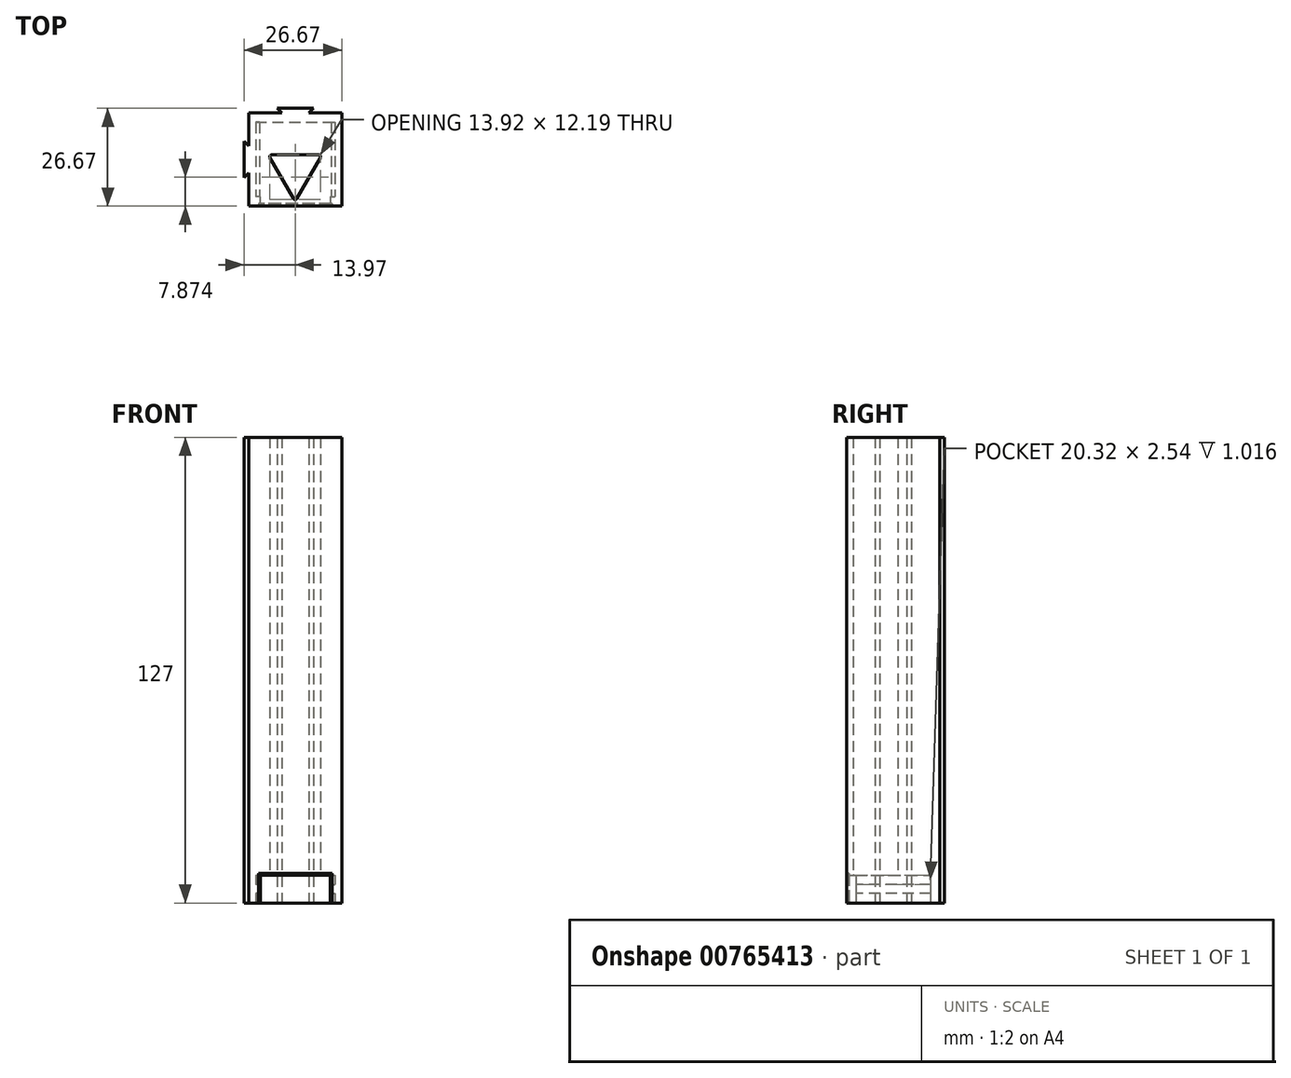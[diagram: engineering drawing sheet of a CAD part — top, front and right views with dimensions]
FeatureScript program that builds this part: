
annotation { "Feature Type Name" : "Feature", "Feature Type Description" : "" }
export const myFeature = defineFeature(function(context is Context, id is Id, definition is map)
    precondition{}
    {
        {
            var Q0;
            Q0=qCreatedBy(makeId("Top.planeOp"),FACE);
            var sketch = newSketch(context, id + "F0", { "sketchPlane" : qUnion([Q0])});
            skLineSegment(sketch, "E0.bottom", {"start": v(12.7, 12.7) * mm, "end": v(-12.7, 12.7) * mm});
            skLineSegment(sketch, "E0.top", {"start": v(12.7, -12.7) * mm, "end": v(-12.7, -12.7) * mm});
            skLineSegment(sketch, "E0.left", {"start": v(12.7, 12.7) * mm, "end": v(12.7, -12.7) * mm});
            skLineSegment(sketch, "E0.right", {"start": v(-12.7, 12.7) * mm, "end": v(-12.7, -12.7) * mm});
            skPoint(sketch, "E0.middle", {"position": v(0, 0) * mm});
            skLineSegment(sketch, "E1", {"start": v(-3.68, 12.7) * mm, "end": v(-4.95, 13.97) * mm});
            skLineSegment(sketch, "E2", {"start": v(-4.95, 13.97) * mm, "end": v(4.95, 13.97) * mm});
            skLineSegment(sketch, "E3", {"start": v(4.95, 13.97) * mm, "end": v(3.68, 12.7) * mm});
            skLineSegment(sketch, "E4.MirrorCS", {"start": v(-12.7, 3.68) * mm, "end": v(-13.97, 4.95) * mm});
            skLineSegment(sketch, "E5.MirrorCS", {"start": v(-13.97, 4.95) * mm, "end": v(-13.97, -4.95) * mm});
            skLineSegment(sketch, "E6.MirrorCS", {"start": v(-13.97, -4.95) * mm, "end": v(-12.7, -3.68) * mm});
            skLineSegment(sketch, "E7.top", {"start": v(-6.45, 1.27) * mm, "end": v(6.45, 1.27) * mm});
            skPoint(sketch, "E7.middle", {"position": v(0, -5.08) * mm});
            skPoint(sketch, "E8.visualSharp", {"position": v(0, 1.27) * mm});
            skLineSegment(sketch, "E9", {"start": v(-0.44, -10.67) * mm, "end": v(-6.9, 0.5) * mm});
            skLineSegment(sketch, "E10", {"start": v(0.44, -10.67) * mm, "end": v(6.9, 0.5) * mm});
            skPoint(sketch, "E7.left.start.orphan", {"position": v(-7.33, -11.43) * mm});
            skPoint(sketch, "E7.right.start.orphan", {"position": v(7.33, -11.43) * mm});
            skPoint(sketch, "E11.visualSharp", {"position": v(0, -11.43) * mm});
            skArc(sketch, "E11.filletArc", {"start": v(-0.44, -10.67) * mm, "mid": v(0, -10.92) * mm, "end": v(0.44, -10.67) * mm});
            skPoint(sketch, "E12.visualSharp", {"position": v(-7.33, 1.27) * mm});
            skArc(sketch, "E12.filletArc", {"start": v(-6.45, 1.27) * mm, "mid": v(-6.9, 1.02) * mm, "end": v(-6.9, 0.5) * mm});
            skPoint(sketch, "E13.visualSharp", {"position": v(7.33, 1.27) * mm});
            skArc(sketch, "E13.filletArc", {"start": v(6.9, 0.5) * mm, "mid": v(6.9, 1.02) * mm, "end": v(6.45, 1.27) * mm});
            skSolve(sketch);
        }
        {
            var Q0;
            {var subQ1=sQuery(id+"F0.wireOp",EDGE,"E0.top");Q0=makeQuery(id+"F0.imprint","IMPRINT",FACE,{"disambiguationData":[TD([[makeQuery(id+"F0.imprint","IMPRINT",EDGE,{"derivedFrom":subQ1}),-1.0]])]});}
            var Q1;
            {var subQ0=sQuery(id+"F0.wireOp",EDGE,"E4.MirrorCS");Q1=makeQuery(id+"F0.imprint","IMPRINT",FACE,{"disambiguationData":[TD([[makeQuery(id+"F0.imprint","IMPRINT",EDGE,{"derivedFrom":subQ0}),1.0]])]});}
            var Q2;
            {var subQ0=sQuery(id+"F0.wireOp",EDGE,"995b501b-87b1-40df-89db-5718103b703a");Q2=makeQuery(id+"F0.imprint","IMPRINT",FACE,{"disambiguationData":[TD([[makeQuery(id+"F0.imprint","IMPRINT",EDGE,{"derivedFrom":subQ0}),-1.0]])]});}
            var Q3;
            {var subQ0=sQuery(id+"F0.wireOp",EDGE,"E1");Q3=makeQuery(id+"F0.imprint","IMPRINT",FACE,{"disambiguationData":[TD([[makeQuery(id+"F0.imprint","IMPRINT",EDGE,{"derivedFrom":subQ0}),-1.0]])]});}
            var Q4;
            Q4=makeQuery(id+"F0.imprint","IMPRINT",FACE,{"disambiguationData":[TD([[makeQuery(id+"F0.imprint","IMPRINT",EDGE,{"derivedFrom":sQuery(id+"F0.wireOp",EDGE,"E7.bottom")}),1.0]])]});
            var Q5;
            Q5=makeQuery(id+"F0.imprint","IMPRINT",FACE,{"disambiguationData":[TD([[makeQuery(id+"F0.imprint","IMPRINT",EDGE,{"derivedFrom":sQuery(id+"F0.wireOp",EDGE,"311fc631-adf6-4f6f-8443-b1374ca45b62.0")}),-1.0]])]});
            extrude(context, id + "F1", {"entities" : qUnion([Q0, Q1, Q2, Q3, Q4, Q5]), "depth" : 127 * mm, "offsetDistance" : 25.4 * mm});
        }
        {
            var Q0;
            Q0=makeQuery(id+"F1.opExtrude","CAP_FACE",FACE,{"disambiguationData":[OSD([sQuery(id+"F0.wireOp",EDGE,"E0.bottom"),sQuery(id+"F0.wireOp",EDGE,"E0.top"),sQuery(id+"F0.wireOp",EDGE,"E0.left"),sQuery(id+"F0.wireOp",EDGE,"E0.right"),sQuery(id+"F0.wireOp",EDGE,"E1"),sQuery(id+"F0.wireOp",EDGE,"E2"),sQuery(id+"F0.wireOp",EDGE,"E3"),sQuery(id+"F0.wireOp",EDGE,"995b501b-87b1-40df-89db-5718103b703a"),sQuery(id+"F0.wireOp",EDGE,"d9b632a0-34b0-463a-8696-1e9d1799fc8a"),sQuery(id+"F0.wireOp",EDGE,"b3bc504c-1797-48d5-8887-40c9249a8113"),sQuery(id+"F0.wireOp",EDGE,"E4.MirrorCS"),sQuery(id+"F0.wireOp",EDGE,"E5.MirrorCS"),sQuery(id+"F0.wireOp",EDGE,"E6.MirrorCS"),sQuery(id+"F0.wireOp",EDGE,"Ek69CNRn-8RVK-RxQl-53fH-Jz5PkY7OIrkr")])],"isStart":true});
            var sketch = newSketch(context, id + "F2", { "sketchPlane" : qUnion([Q0])});
            skLineSegment(sketch, "E14", {"start": v(-9.52, 12.7) * mm, "end": v(-9.52, 10.16) * mm});
            skLineSegment(sketch, "E15", {"start": v(-9.52, 10.16) * mm, "end": v(-10.8, 10.16) * mm});
            skLineSegment(sketch, "E16", {"start": v(-10.8, 10.16) * mm, "end": v(-10.8, -10.16) * mm});
            skLineSegment(sketch, "E17", {"start": v(-10.8, -10.16) * mm, "end": v(10.8, -10.16) * mm});
            skLineSegment(sketch, "E18", {"start": v(10.8, -10.16) * mm, "end": v(10.8, 10.16) * mm});
            skLineSegment(sketch, "E19", {"start": v(9.52, 10.16) * mm, "end": v(10.8, 10.16) * mm});
            skLineSegment(sketch, "E20", {"start": v(9.52, 10.16) * mm, "end": v(9.52, 12.7) * mm});
            skLineSegment(sketch, "E21", {"start": v(9.52, 12.7) * mm, "end": v(-9.52, 12.7) * mm});
            skSolve(sketch);
        }
        {
            var Q0;
            Q0=makeQuery(id+"F2.imprint","IMPRINT",FACE,{"disambiguationData":[TD([[makeQuery(id+"F2.imprint","IMPRINT",EDGE,{"derivedFrom":sQuery(id+"F2.wireOp",EDGE,"E14")}),1.0]])]});
            extrude(context, id + "F3", {"entities" : qUnion([Q0]), "operationType" : NewBodyOperationType.REMOVE, "oppositeDirection" : true, "depth" : 7.62 * mm, "offsetDistance" : 25.4 * mm});
        }
        {
            var Q0;
            Q0=makeQuery(id+"F1.opExtrude","SWEPT_FACE",FACE,{"disambiguationData":[OSD([sQuery(id+"F0.wireOp",EDGE,"E0.top")])]});
            var sketch = newSketch(context, id + "F4", { "sketchPlane" : qUnion([Q0])});
            skLineSegment(sketch, "E22.0", {"start": v(-10.03, 8.13) * mm, "end": v(-10.03, 0) * mm});
            skLineSegment(sketch, "E22.1", {"start": v(10.03, 8.13) * mm, "end": v(-10.03, 8.13) * mm});
            skLineSegment(sketch, "E22.2", {"start": v(10.03, 8.13) * mm, "end": v(10.03, 0) * mm});
            skSolve(sketch);
        }
        {
            var Q0;
            {var subQ13=sQuery(id+"F4.wireOp",EDGE,"E22.0");Q0=makeQuery(id+"F4.imprint","IMPRINT",FACE,{"disambiguationData":[TD([[makeQuery(id+"F4.imprint","IMPRINT",EDGE,{"derivedFrom":subQ13}),1.0]])]});}
            extrude(context, id + "F5", {"entities" : qUnion([Q0]), "operationType" : NewBodyOperationType.REMOVE, "oppositeDirection" : true, "depth" : 0.64 * mm, "offsetDistance" : 25.4 * mm});
        }
        {
            var Q0;
            Q0=makeQuery(id+"F3.boolean.opBoolean","COPY",FACE,{"derivedFrom":makeQuery(id+"F3.opExtrude","SWEPT_FACE",FACE,{"disambiguationData":[OSD([sQuery(id+"F2.wireOp",EDGE,"E16")])]})});
            var sketch = newSketch(context, id + "F6", { "sketchPlane" : qUnion([Q0])});
            skLineSegment(sketch, "E23.bottom", {"start": v(10.16, 5.08) * mm, "end": v(-10.16, 5.08) * mm});
            skLineSegment(sketch, "E23.top", {"start": v(10.16, 2.67) * mm, "end": v(-10.16, 2.67) * mm});
            skLineSegment(sketch, "E23.left", {"start": v(10.16, 5.08) * mm, "end": v(10.16, 2.67) * mm});
            skLineSegment(sketch, "E23.right", {"start": v(-10.16, 5.08) * mm, "end": v(-10.16, 2.67) * mm});
            skSolve(sketch);
        }
        {
            var Q0;
            Q0=makeQuery(id+"F6.imprint","IMPRINT",FACE,{"disambiguationData":[TD([[makeQuery(id+"F6.imprint","IMPRINT",EDGE,{"derivedFrom":sQuery(id+"F6.wireOp",EDGE,"E23.bottom")}),1.0]])]});
            extrude(context, id + "F7", {"entities" : qUnion([Q0]), "depth" : 1.02 * mm, "offsetDistance" : 25.4 * mm});
        }
        {
            var Q0;
            Q0=makeQuery(id+"F7.opExtrude","SWEPT_BODY",BODY,{"disambiguationData":[OSD([sQuery(id+"F6.wireOp",EDGE,"E23.bottom"),sQuery(id+"F6.wireOp",EDGE,"E23.top"),sQuery(id+"F6.wireOp",EDGE,"E23.left"),sQuery(id+"F6.wireOp",EDGE,"E23.right")])]});
            var Q1;
            Q1=qCreatedBy(makeId("Right.planeOp"),FACE);
            mirror(context, id + "F8", {"operationType" : NewBodyOperationType.ADD, "entities" : qUnion([Q0]), "mirrorPlane" : qUnion([Q1])});
        }
        {
            var Q0;
            Q0=makeQuery(id+"F1.opExtrude","SWEPT_BODY",BODY,{"disambiguationData":[OSD([sQuery(id+"F0.wireOp",EDGE,"E0.bottom"),sQuery(id+"F0.wireOp",EDGE,"E0.top"),sQuery(id+"F0.wireOp",EDGE,"E0.left"),sQuery(id+"F0.wireOp",EDGE,"E0.right"),sQuery(id+"F0.wireOp",EDGE,"E1"),sQuery(id+"F0.wireOp",EDGE,"E2"),sQuery(id+"F0.wireOp",EDGE,"E3"),sQuery(id+"F0.wireOp",EDGE,"995b501b-87b1-40df-89db-5718103b703a"),sQuery(id+"F0.wireOp",EDGE,"d9b632a0-34b0-463a-8696-1e9d1799fc8a"),sQuery(id+"F0.wireOp",EDGE,"b3bc504c-1797-48d5-8887-40c9249a8113"),sQuery(id+"F0.wireOp",EDGE,"E4.MirrorCS"),sQuery(id+"F0.wireOp",EDGE,"E5.MirrorCS"),sQuery(id+"F0.wireOp",EDGE,"E6.MirrorCS"),sQuery(id+"F0.wireOp",EDGE,"Ek69CNRn-8RVK-RxQl-53fH-Jz5PkY7OIrkr")])]});
            transform(context, id + "F9", {"entities" : qUnion([Q0]), "transformType" : TransformType.TRANSLATION_3D, "dx" : 0 * mm, "dy" : 0 * mm, "dz" : 0 * mm, "makeCopy" : true});
        }
        {
            var Q0;
            Q0=makeQuery(id+"F9.opPattern","COPY",BODY,{"derivedFrom":makeQuery(id+"F1.opExtrude","SWEPT_BODY",BODY,{"disambiguationData":[OSD([sQuery(id+"F0.wireOp",EDGE,"E0.bottom"),sQuery(id+"F0.wireOp",EDGE,"E0.top"),sQuery(id+"F0.wireOp",EDGE,"E0.left"),sQuery(id+"F0.wireOp",EDGE,"E0.right"),sQuery(id+"F0.wireOp",EDGE,"E1"),sQuery(id+"F0.wireOp",EDGE,"E2"),sQuery(id+"F0.wireOp",EDGE,"E3"),sQuery(id+"F0.wireOp",EDGE,"995b501b-87b1-40df-89db-5718103b703a"),sQuery(id+"F0.wireOp",EDGE,"d9b632a0-34b0-463a-8696-1e9d1799fc8a"),sQuery(id+"F0.wireOp",EDGE,"b3bc504c-1797-48d5-8887-40c9249a8113"),sQuery(id+"F0.wireOp",EDGE,"E4.MirrorCS"),sQuery(id+"F0.wireOp",EDGE,"E5.MirrorCS"),sQuery(id+"F0.wireOp",EDGE,"E6.MirrorCS"),sQuery(id+"F0.wireOp",EDGE,"E7.top"),sQuery(id+"F0.wireOp",EDGE,"E9"),sQuery(id+"F0.wireOp",EDGE,"E10"),sQuery(id+"F0.wireOp",EDGE,"E11.filletArc"),sQuery(id+"F0.wireOp",EDGE,"E12.filletArc"),sQuery(id+"F0.wireOp",EDGE,"E13.filletArc")])]}),"instanceName":"1"});
            deleteBodies(context, id + "F10", {"entities" : qUnion([Q0])});
        }
    });
